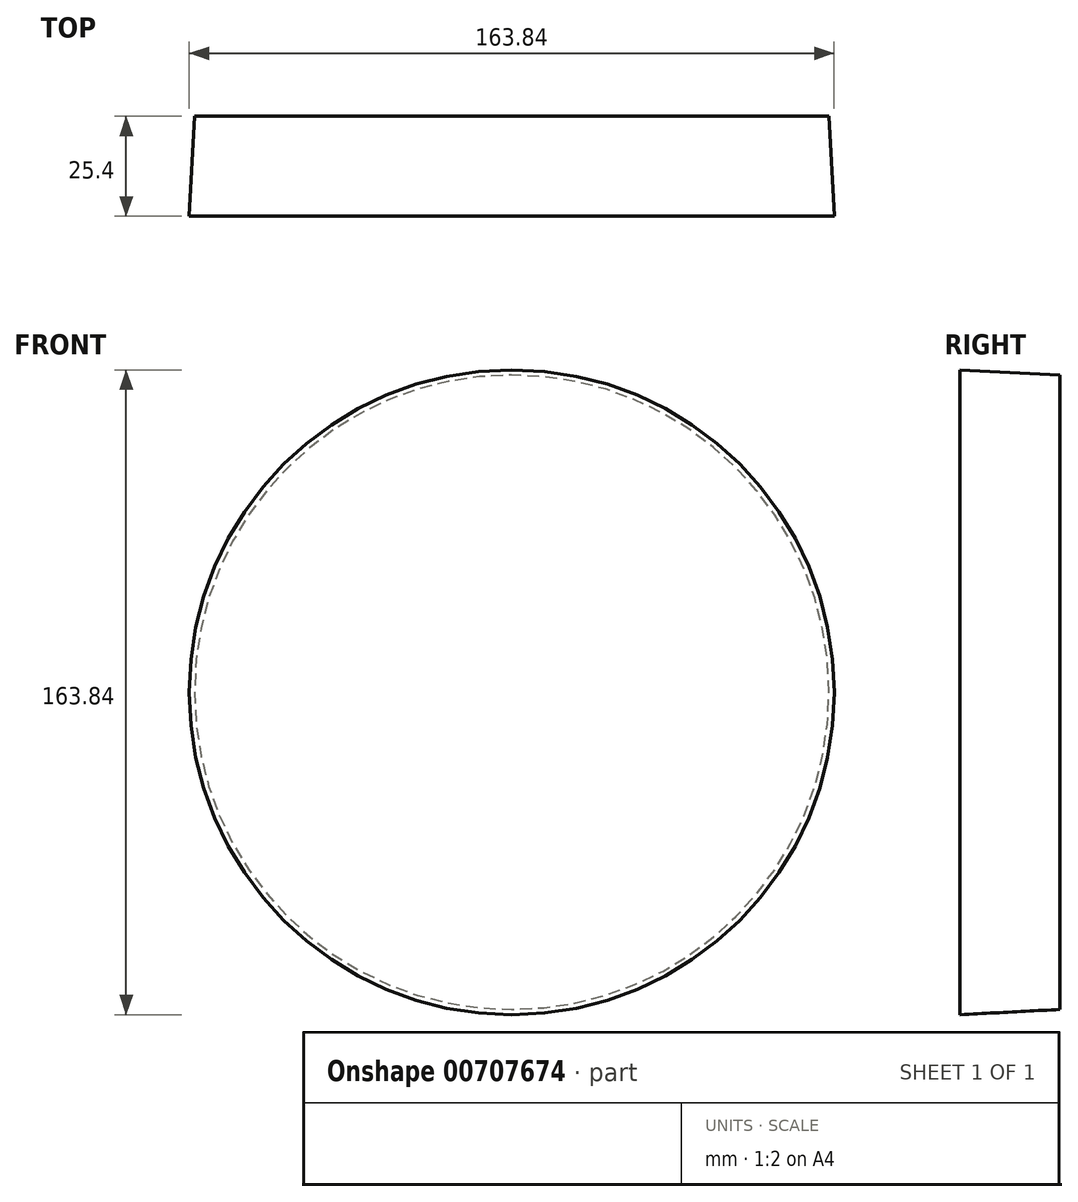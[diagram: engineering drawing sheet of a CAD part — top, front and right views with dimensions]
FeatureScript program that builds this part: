
annotation { "Feature Type Name" : "Feature", "Feature Type Description" : "" }
export const myFeature = defineFeature(function(context is Context, id is Id, definition is map)
    precondition{}
    {
        {
            var Q0;
            Q0=qCreatedBy(makeId("Front.planeOp"),FACE);
            var sketch = newSketch(context, id + "F0", { "sketchPlane" : qUnion([Q0])});
            skCircle(sketch, "E0", {"center": v(0, 0) * mm, "radius": 80.6 * mm});
            skSolve(sketch);
        }
        {
            var Q0;
            Q0=makeQuery(id+"F0.imprint","IMPRINT",FACE,{"disambiguationData":[TD([[makeQuery(id+"F0.imprint","IMPRINT",EDGE,{"derivedFrom":sQuery(id+"F0.wireOp",EDGE,"E0")}),1.0]])]});
            extrude(context, id + "F1", {"entities" : qUnion([Q0]), "depth" : 25.4 * mm, "offsetDistance" : 25.4 * mm, "hasDraft" : true, "draftAngle" : 3 * degree});
        }
    });
